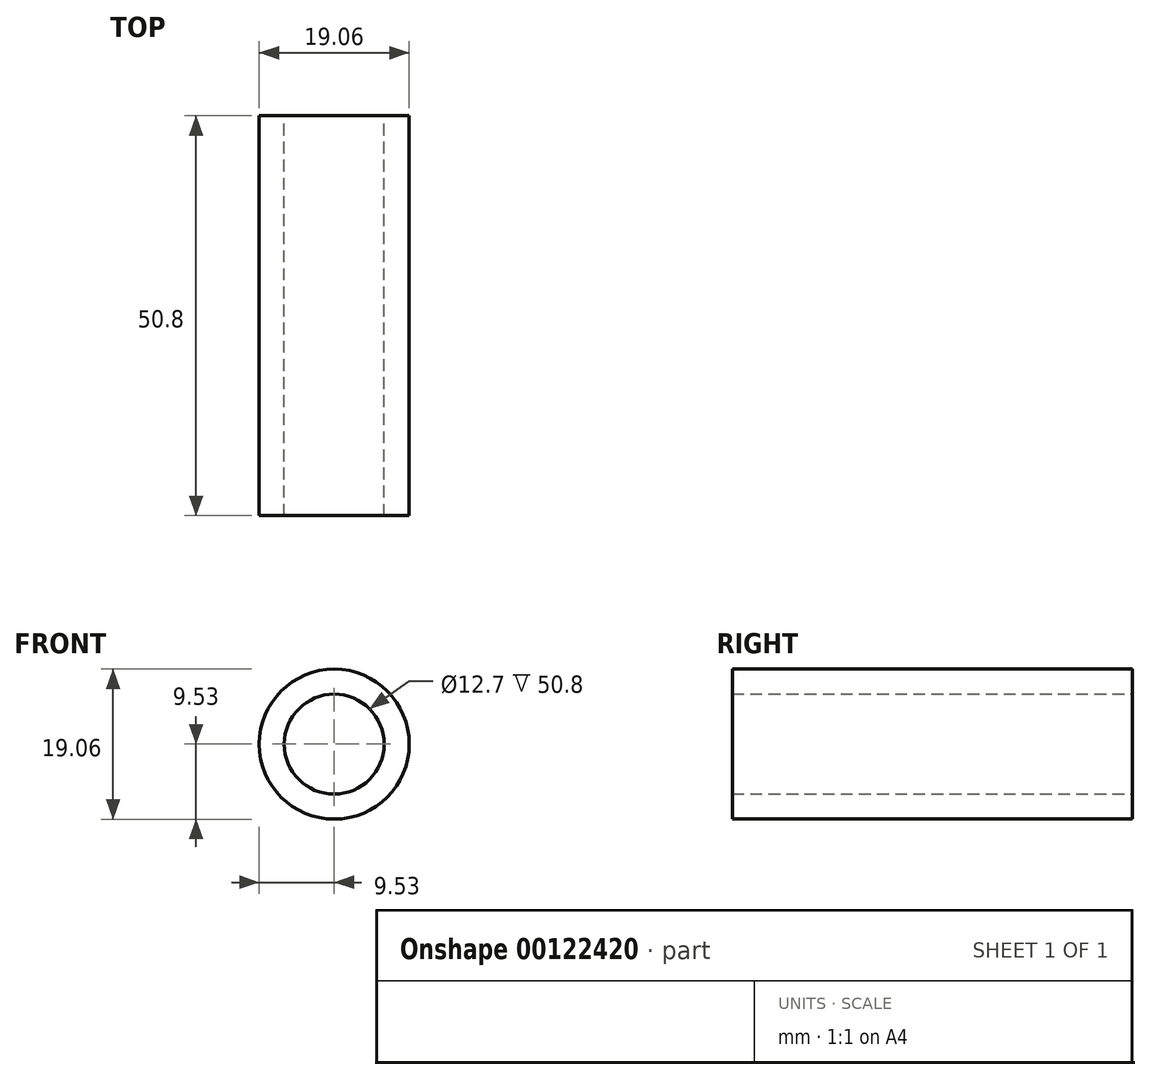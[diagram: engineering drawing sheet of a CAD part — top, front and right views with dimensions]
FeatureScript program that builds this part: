
annotation { "Feature Type Name" : "Feature", "Feature Type Description" : "" }
export const myFeature = defineFeature(function(context is Context, id is Id, definition is map)
    precondition{}
    {
        {
            var Q0;
            Q0=qCreatedBy(makeId("Front.planeOp"),FACE);
            var sketch = newSketch(context, id + "F0", { "sketchPlane" : qUnion([Q0])});
            skCircle(sketch, "E0", {"center": v(0, 0) * mm, "radius": 9.53 * mm});
            skCircle(sketch, "E1", {"center": v(0, 0) * mm, "radius": 6.35 * mm});
            skSolve(sketch);
        }
        {
            var Q0;
            Q0 = qSketchRegion(id + "F0", true);
            extrude(context, id + "F1", {"entities" : qUnion([Q0]), "offsetDistance" : 25.4 * mm, "depth" : 50.8 * mm});
        }
    });
